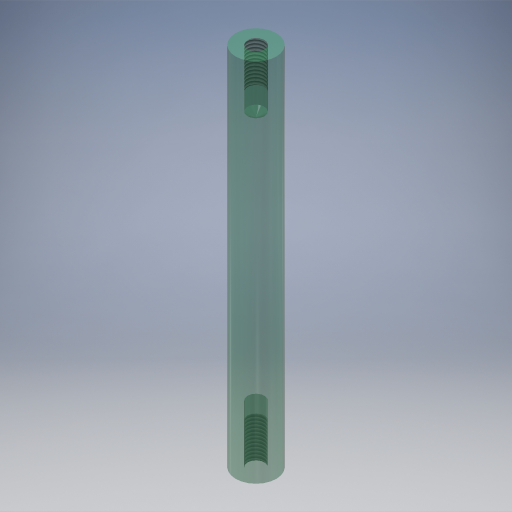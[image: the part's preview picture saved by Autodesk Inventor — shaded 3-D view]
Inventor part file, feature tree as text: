
AUTODESK INVENTOR PART (.ipt)
format: ipt  version: 2024.3 (Build 283343000, 343)  size: 290,304 bytes
history: native  units: mm
features: hole x2, sketch x2, extrude x1
ambient origin geometry x8: Origin, YZ Plane, XZ Plane, XY Plane, X Axis, Y Axis, Z Axis, Center Point
bodies: Volumenkörper1 (feature_tree)
feature tree (5):
  extrude  "Extrusion1"  Depth=90.0mm TaperAngle=0.0deg
  hole  "Bohrung1"  [1 undecoded]
  hole  "Bohrung2"  [1 undecoded]
  sketch  "Skizze2"  dims[d0=10.0mm d1=90.0mm d2=0.0mm]
  sketch  "Skizze3"  dims[d3=4.134mm d4=10.0mm d5=4.0mm d6=2.0mm d7=90.0deg d8=14.2mm d9=20.594885mm d10=4.134mm d11=10.0mm d12=4.0mm d13=2.0mm d14=90.0deg d15=14.2mm d16=20.594885mm]
note: 2 required parameter values undecoded (feature->parameter linkage not recoverable at this tier; creation-order binding heuristic only, values carry confidence <= 0.55)
